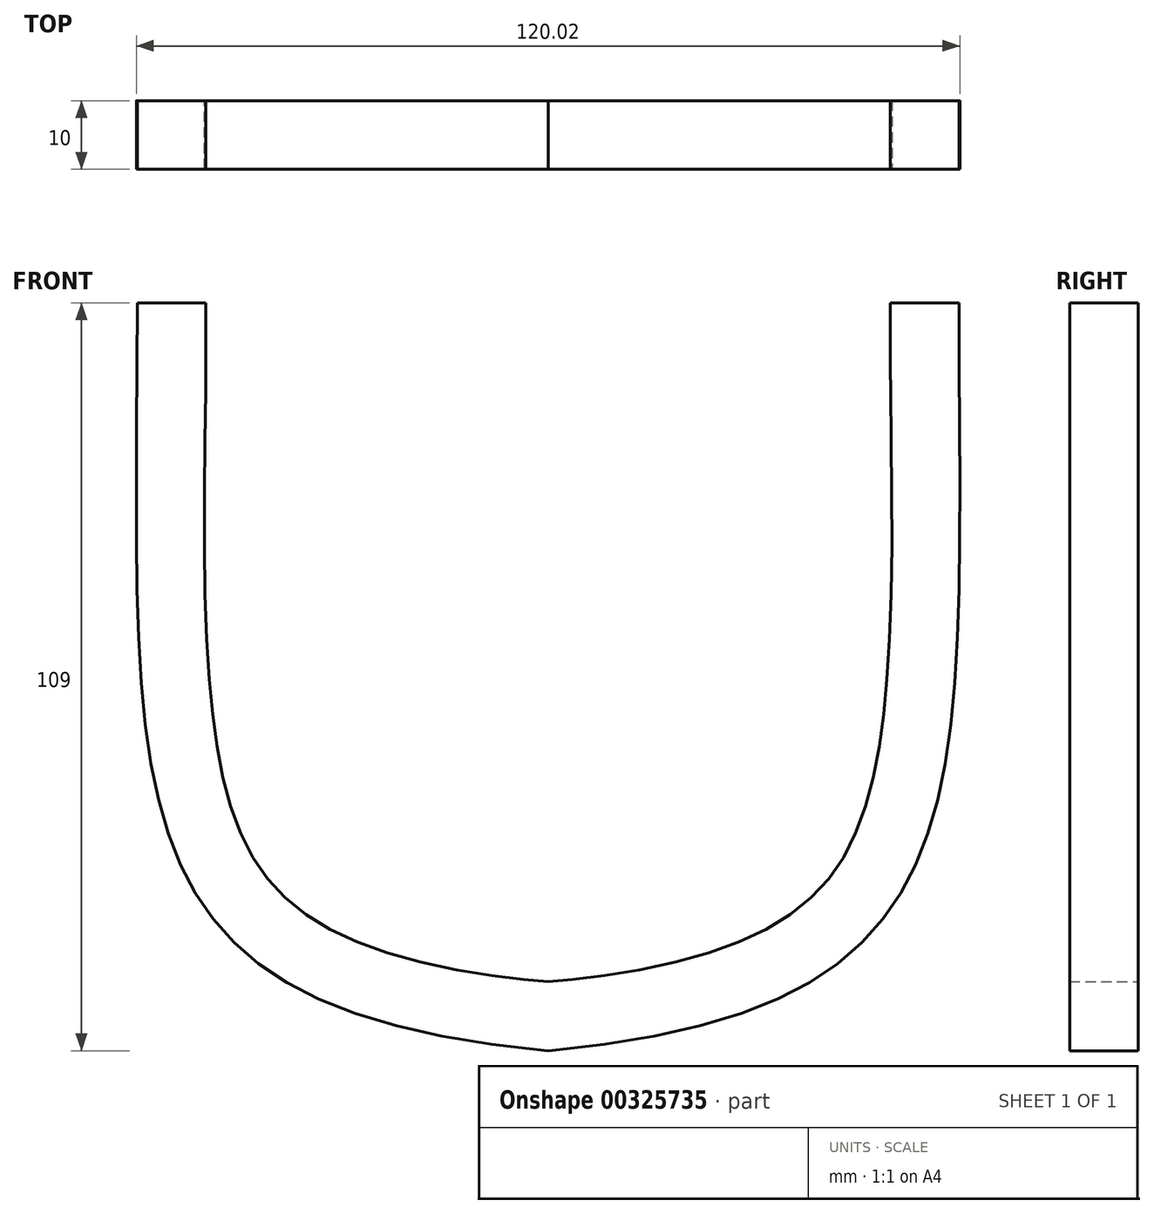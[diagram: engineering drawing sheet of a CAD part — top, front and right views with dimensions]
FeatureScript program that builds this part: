
annotation { "Feature Type Name" : "Feature", "Feature Type Description" : "" }
export const myFeature = defineFeature(function(context is Context, id is Id, definition is map)
    precondition{}
    {
        {
            var Q0;
            Q0=qCreatedBy(makeId("Front.planeOp"),FACE);
            var sketch = newSketch(context, id + "F0", { "sketchPlane" : qUnion([Q0])});
            skLineSegment(sketch, "E0", {"start": v(-60.11, 0) * mm, "end": v(59.89, 0) * mm, "construction": true});
            skLineSegment(sketch, "E1", {"start": v(59.89, 0) * mm, "end": v(59.89, 109) * mm, "construction": true});
            skLineSegment(sketch, "E2", {"start": v(0, 0) * mm, "end": v(0, 110.18) * mm});
            skFitSpline(sketch, "E3", {"points": [v(0, 0) * mm, v(59.89, 109) * mm], "startDerivative": vector(196.47, 18.55) * mm, "endDerivative": vector(0, 219.91) * mm});
            skFitSpline(sketch, "E4.MirrorCS", {"points": [v(0, 0) * mm, v(-59.89, 109) * mm], "startDerivative": vector(-196.47, 18.55) * mm, "endDerivative": vector(0, 219.91) * mm});
            skFitSpline(sketch, "E5.0", {"points": [v(0.94, 9.96) * mm, v(-2.96, 10.32) * mm, v(-10.16, 11.23) * mm, v(-19.21, 13.07) * mm, v(-26.58, 15.37) * mm, v(-32.39, 18.04) * mm, v(-36.85, 21.02) * mm, v(-40.28, 24.33) * mm, v(-43.02, 28.16) * mm, v(-45.27, 32.8) * mm, v(-47.06, 38.47) * mm, v(-48.4, 45.24) * mm, v(-49.29, 53.13) * mm, v(-49.97, 65.1) * mm, v(-50.06, 82.78) * mm, v(-49.89, 99.77) * mm, v(-49.89, 109) * mm]});
            skFitSpline(sketch, "E6.0", {"points": [v(-0.94, 9.96) * mm, v(2.96, 10.32) * mm, v(10.16, 11.23) * mm, v(19.21, 13.07) * mm, v(26.58, 15.37) * mm, v(32.39, 18.04) * mm, v(36.85, 21.02) * mm, v(40.28, 24.33) * mm, v(43.02, 28.16) * mm, v(45.27, 32.8) * mm, v(47.06, 38.47) * mm, v(48.4, 45.24) * mm, v(49.29, 53.13) * mm, v(49.97, 65.1) * mm, v(50.06, 82.78) * mm, v(49.89, 99.77) * mm, v(49.89, 109) * mm]});
            skLineSegment(sketch, "E7", {"start": v(-59.89, 109) * mm, "end": v(-49.89, 109) * mm});
            skLineSegment(sketch, "E8", {"start": v(49.89, 109) * mm, "end": v(59.89, 109) * mm});
            skPoint(sketch, "E9", {"position": v(-49.9, 106.13) * mm});
            skPoint(sketch, "E10", {"position": v(49.89, 106.13) * mm});
            skPoint(sketch, "E11", {"position": v(49.93, 96.13) * mm});
            skPoint(sketch, "E12", {"position": v(-49.93, 96.13) * mm});
            skPoint(sketch, "E13", {"position": v(-50, 82.63) * mm});
            skPoint(sketch, "E14", {"position": v(50, 82.63) * mm});
            skPoint(sketch, "E15", {"position": v(-31.72, 96.13) * mm});
            skPoint(sketch, "E16", {"position": v(31.72, 96.13) * mm});
            skLineSegment(sketch, "E17", {"start": v(-49.93, 96.13) * mm, "end": v(-31.72, 96.13) * mm});
            skLineSegment(sketch, "E18", {"start": v(-50, 82.63) * mm, "end": v(-31.72, 96.13) * mm});
            skLineSegment(sketch, "E19", {"start": v(31.72, 96.13) * mm, "end": v(49.93, 96.13) * mm});
            skLineSegment(sketch, "E20", {"start": v(31.72, 96.13) * mm, "end": v(50, 82.63) * mm});
            skSolve(sketch);
        }
        {
            var Q0;
            Q0 = qSketchRegion(id + "F0", true);
            extrude(context, id + "F1", {"entities" : qUnion([Q0]), "endBound" : BoundingType.SYMMETRIC, "depth" : 10 * mm});
        }
    });
